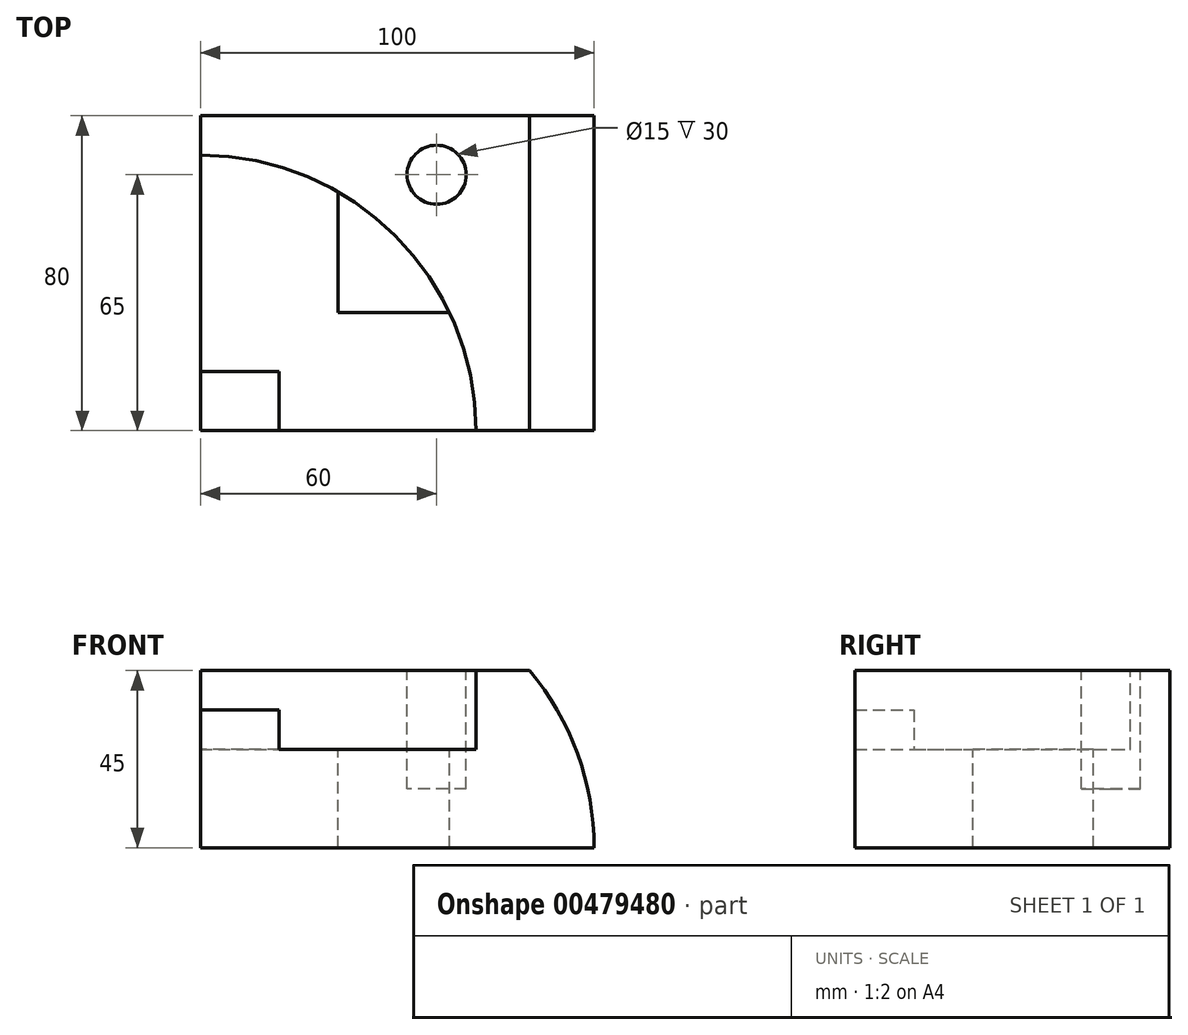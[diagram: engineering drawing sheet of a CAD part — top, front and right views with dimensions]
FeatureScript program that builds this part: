
annotation { "Feature Type Name" : "Feature", "Feature Type Description" : "" }
export const myFeature = defineFeature(function(context is Context, id is Id, definition is map)
    precondition{}
    {
        {
            var Q0;
            Q0=qCreatedBy(makeId("Front.planeOp"),FACE);
            var sketch = newSketch(context, id + "F0", { "sketchPlane" : qUnion([Q0])});
            skLineSegment(sketch, "E0.bottom", {"start": v(0, 0) * mm, "end": v(100, 0) * mm});
            skLineSegment(sketch, "E0.top", {"start": v(0, 45) * mm, "end": v(100, 45) * mm});
            skLineSegment(sketch, "E0.left", {"start": v(0, 0) * mm, "end": v(0, 45) * mm});
            skLineSegment(sketch, "E0.right", {"start": v(100, 0) * mm, "end": v(100, 45) * mm});
            skSolve(sketch);
        }
        {
            var Q0;
            Q0 = qSketchRegion(id + "F0", true);
            extrude(context, id + "F1", {"entities" : qUnion([Q0]), "depth" : 80 * mm});
        }
        {
            var Q0;
            Q0=makeQuery(id+"F1.opExtrude","SWEPT_FACE",FACE,{"disambiguationData":[OSD([sQuery(id+"F0.wireOp",EDGE,"E0.top")])]});
            var sketch = newSketch(context, id + "F2", { "sketchPlane" : qUnion([Q0])});
            skCircle(sketch, "E1", {"center": v(60, -15) * mm, "radius": 7.5 * mm});
            skSolve(sketch);
        }
        {
            var Q0;
            Q0 = qSketchRegion(id + "F2", true);
            extrude(context, id + "F3", {"entities" : qUnion([Q0]), "operationType" : NewBodyOperationType.REMOVE, "oppositeDirection" : true, "depth" : 30 * mm});
        }
        {
            var Q0;
            Q0=makeQuery(id+"F1.opExtrude","SWEPT_FACE",FACE,{"disambiguationData":[OSD([sQuery(id+"F0.wireOp",EDGE,"E0.top")])]});
            var sketch = newSketch(context, id + "F4", { "sketchPlane" : qUnion([Q0])});
            skCircle(sketch, "E2", {"center": v(0, -80) * mm, "radius": 70 * mm});
            skSolve(sketch);
        }
        {
            var Q0;
            Q0 = qSketchRegion(id + "F4", true);
            extrude(context, id + "F5", {"entities" : qUnion([Q0]), "operationType" : NewBodyOperationType.REMOVE, "oppositeDirection" : true, "depth" : 20 * mm});
        }
        {
            var Q0;
            Q0=makeQuery(id+"F5.boolean.opBoolean","COPY",FACE,{"derivedFrom":makeQuery(id+"F5.opExtrude","CAP_FACE",FACE,{"disambiguationData":[OSD([sQuery(id+"F4.wireOp",EDGE,"E2")])],"isStart":false})});
            var sketch = newSketch(context, id + "F6", { "sketchPlane" : qUnion([Q0])});
            skLineSegment(sketch, "E3.bottom", {"start": v(0, -80) * mm, "end": v(20, -80) * mm});
            skLineSegment(sketch, "E3.top", {"start": v(0, -65) * mm, "end": v(20, -65) * mm});
            skLineSegment(sketch, "E3.left", {"start": v(0, -80) * mm, "end": v(0, -65) * mm});
            skLineSegment(sketch, "E3.right", {"start": v(20, -80) * mm, "end": v(20, -65) * mm});
            skSolve(sketch);
        }
        {
            var Q0;
            Q0 = qSketchRegion(id + "F6", true);
            extrude(context, id + "F7", {"entities" : qUnion([Q0]), "operationType" : NewBodyOperationType.ADD, "depth" : 10 * mm});
        }
        {
            var Q0;
            Q0=makeQuery(id+"F5.boolean.opBoolean","COPY",FACE,{"derivedFrom":makeQuery(id+"F5.opExtrude","CAP_FACE",FACE,{"disambiguationData":[OSD([sQuery(id+"F4.wireOp",EDGE,"E2")])],"isStart":false})});
            var sketch = newSketch(context, id + "F8", { "sketchPlane" : qUnion([Q0])});
            skSolve(sketch);
        }
        {
            var Q0;
            {var subQ0=sQuery(id+"F4.wireOp",EDGE,"E2");Q0=makeQuery(id+"F8.imprint","IMPRINT",FACE,{"disambiguationData":[TD([[makeQuery(id+"F8.imprint","IMPRINT",EDGE,{"derivedFrom":makeQuery(id+"F5.boolean.opBoolean","COPY",EDGE,{"derivedFrom":makeQuery(id+"F5.opExtrude","CAP_EDGE",EDGE,{"disambiguationData":[OSD([subQ0])],"isStart":false})})}),1.0]])]});}
            var sketch = newSketch(context, id + "F9", { "sketchPlane" : qUnion([Q0])});
            skLineSegment(sketch, "E4", {"start": v(35, -19.38) * mm, "end": v(35, -50) * mm});
            skLineSegment(sketch, "E5", {"start": v(35, -50) * mm, "end": v(63.25, -50) * mm});
            skSolve(sketch);
        }
        {
            var Q0;
            Q0 = qSketchRegion(id + "F9", true);
            var Q1;
            {var subQ0=sQuery(id+"F9.wireOp",EDGE,"E4");Q1=makeQuery(id+"F9.imprint","IMPRINT",FACE,{"disambiguationData":[TD([[makeQuery(id+"F9.imprint","IMPRINT",EDGE,{"derivedFrom":subQ0}),1.0]])]});}
            extrude(context, id + "F10", {"entities" : qUnion([Q0, Q1]), "operationType" : NewBodyOperationType.REMOVE, "endBound" : BoundingType.THROUGH_ALL, "oppositeDirection" : true, "depth" : 25 * mm});
        }
        {
            var Q0;
            Q0=makeQuery(id+"F7.boolean.opBoolean","MERGE",FACE,{"derivedFrom":[makeQuery(id+"F1.opExtrude","CAP_FACE",FACE,{"disambiguationData":[OSD([sQuery(id+"F0.wireOp",EDGE,"E0.bottom"),sQuery(id+"F0.wireOp",EDGE,"E0.top"),sQuery(id+"F0.wireOp",EDGE,"E0.left"),sQuery(id+"F0.wireOp",EDGE,"E0.right")])],"isStart":false}),makeQuery(id+"F7.opExtrude","SWEPT_FACE",FACE,{"disambiguationData":[OSD([sQuery(id+"F6.wireOp",EDGE,"E3.bottom")])]})]});
            var sketch = newSketch(context, id + "F11", { "sketchPlane" : qUnion([Q0])});
            skCircle(sketch, "E6", {"center": v(30, 0) * mm, "radius": 70 * mm});
            skSolve(sketch);
        }
        {
            var Q0;
            {var subQ1=makeQuery(id+"F1.opExtrude","CAP_EDGE",EDGE,{"disambiguationData":[OSD([sQuery(id+"F0.wireOp",EDGE,"E0.right")])],"isStart":false});Q0=makeQuery(id+"F11.imprint","IMPRINT",FACE,{"disambiguationData":[TD([[makeQuery(id+"F11.imprint","IMPRINT",EDGE,{"derivedFrom":subQ1}),1.0]])]});}
            extrude(context, id + "F12", {"entities" : qUnion([Q0]), "operationType" : NewBodyOperationType.REMOVE, "endBound" : BoundingType.THROUGH_ALL, "oppositeDirection" : true, "depth" : 25 * mm});
        }
    });
